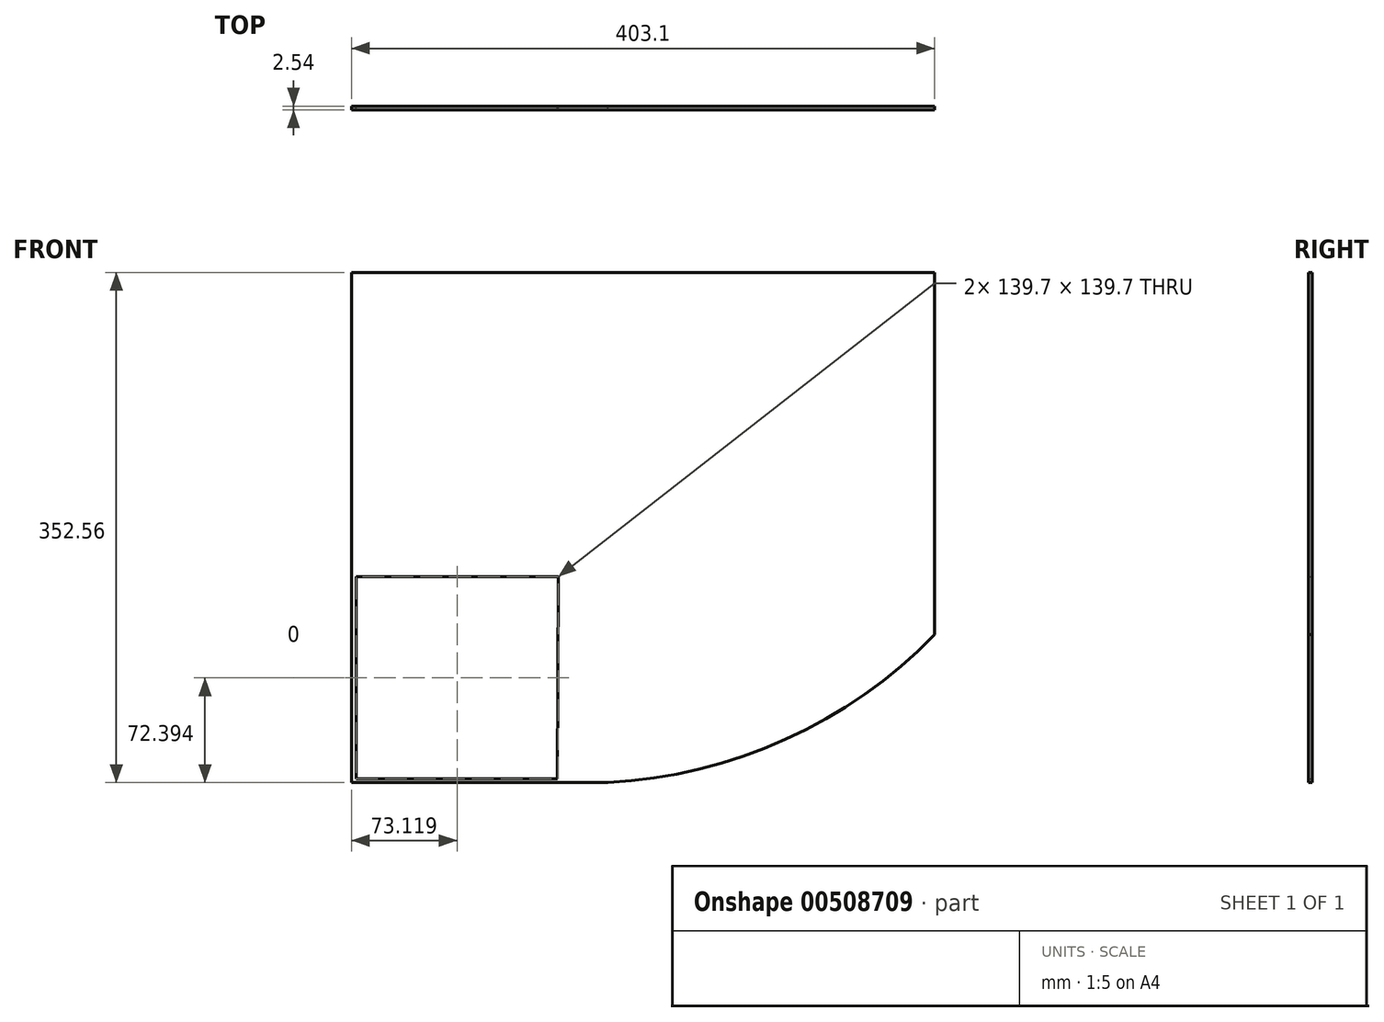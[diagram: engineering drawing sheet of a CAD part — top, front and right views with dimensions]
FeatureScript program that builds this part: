
annotation { "Feature Type Name" : "Feature", "Feature Type Description" : "" }
export const myFeature = defineFeature(function(context is Context, id is Id, definition is map)
    precondition{}
    {
        {
            var Q0;
            Q0=qCreatedBy(makeId("Front.planeOp"),FACE);
            var sketch = newSketch(context, id + "F0", { "sketchPlane" : qUnion([Q0])});
            skLineSegment(sketch, "E0", {"start": v(0, 200.68) * mm, "end": v(0, -151.88) * mm});
            skLineSegment(sketch, "E1", {"start": v(0, -151.88) * mm, "end": v(403.1, -151.88) * mm});
            skLineSegment(sketch, "E2", {"start": v(403.1, -151.88) * mm, "end": v(403.1, 200.68) * mm});
            skLineSegment(sketch, "E3", {"start": v(403.1, 200.68) * mm, "end": v(0, 200.68) * mm});
            skLineSegment(sketch, "E4", {"start": v(142.24, -149.33) * mm, "end": v(3.27, -149.34) * mm});
            skArc(sketch, "E5", {"start": v(142.24, -149.33) * mm, "mid": v(284.68, -127.36) * mm, "end": v(403.1, -45.2) * mm});
            skArc(sketch, "E6", {"start": v(142.24, -151.88) * mm, "mid": v(283.7, -128.93) * mm, "end": v(403.1, -49.67) * mm});
            skLineSegment(sketch, "E7", {"start": v(3.27, -149.34) * mm, "end": v(3.27, -9.64) * mm});
            skLineSegment(sketch, "E8", {"start": v(3.27, -9.64) * mm, "end": v(142.97, -9.64) * mm});
            skLineSegment(sketch, "E9", {"start": v(142.97, -9.64) * mm, "end": v(142.24, -149.33) * mm});
            skSolve(sketch);
        }
        {
            var Q0;
            Q0=makeQuery(id+"F0.imprint","IMPRINT",FACE,{"disambiguationData":[TD([[makeQuery(id+"F0.imprint","IMPRINT",EDGE,{"derivedFrom":sQuery(id+"F0.wireOp",EDGE,"E0")}),1.0]])]});
            extrude(context, id + "F1", {"entities" : qUnion([Q0]), "depth" : 2.54 * mm});
        }
    });
